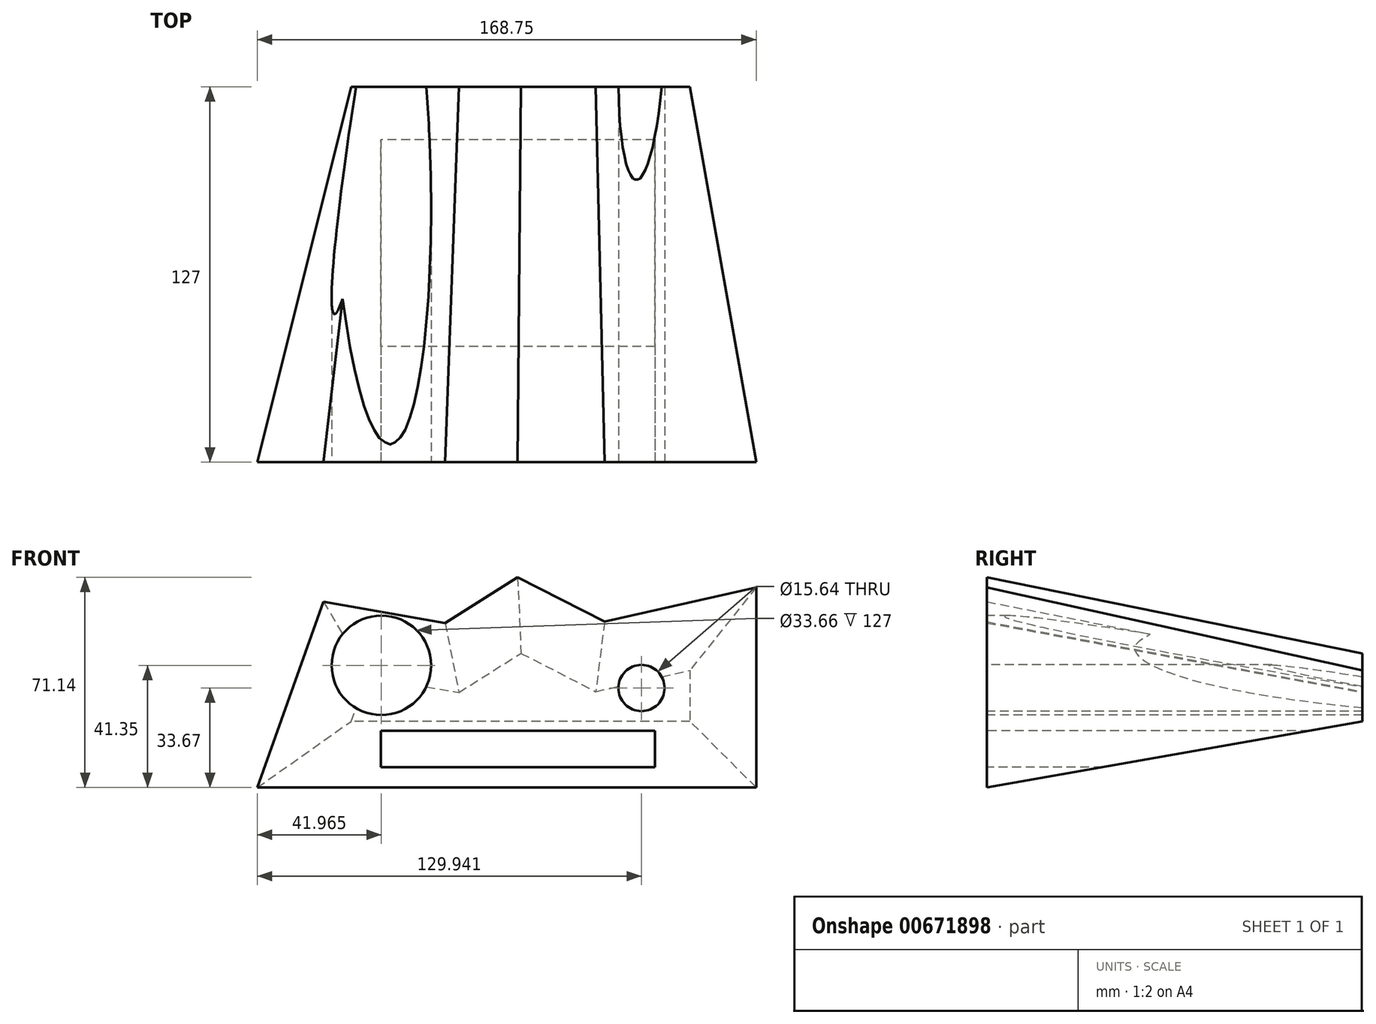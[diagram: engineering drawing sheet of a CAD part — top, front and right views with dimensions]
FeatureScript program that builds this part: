
annotation { "Feature Type Name" : "Feature", "Feature Type Description" : "" }
export const myFeature = defineFeature(function(context is Context, id is Id, definition is map)
    precondition{}
    {
        {
            var Q0;
            Q0=qCreatedBy(makeId("Front.planeOp"),FACE);
            var sketch = newSketch(context, id + "F0", { "sketchPlane" : qUnion([Q0])});
            skLineSegment(sketch, "E0", {"start": v(-47.37, 15.19) * mm, "end": v(-16.4, 9.78) * mm});
            skLineSegment(sketch, "E1", {"start": v(-16.4, 9.78) * mm, "end": v(4.66, 23.01) * mm});
            skLineSegment(sketch, "E2", {"start": v(4.66, 23.01) * mm, "end": v(29.93, 10.08) * mm});
            skLineSegment(sketch, "E3", {"start": v(29.93, 10.08) * mm, "end": v(61.81, 17.3) * mm});
            skLineSegment(sketch, "E4", {"start": v(61.81, 17.3) * mm, "end": v(61.81, 0) * mm});
            skLineSegment(sketch, "E5", {"start": v(61.81, 0) * mm, "end": v(-52.79, 0) * mm});
            skLineSegment(sketch, "E6", {"start": v(-52.79, 0) * mm, "end": v(-47.37, 15.19) * mm});
            skSolve(sketch);
        }
        {
            var Q0;
            Q0=makeQuery(id+"F0.imprint","IMPRINT",FACE,{"disambiguationData":[TD([[makeQuery(id+"F0.imprint","IMPRINT",EDGE,{"derivedFrom":sQuery(id+"F0.wireOp",EDGE,"E0")}),-1.0]])]});
            extrude(context, id + "F1", {"entities" : qUnion([Q0]), "depth" : 127 * mm, "offsetDistance" : 25.4 * mm, "hasDraft" : true, "draftAngle" : 10 * degree});
        }
        {
            var Q0;
            Q0=makeQuery(id+"F1.opExtrude","CAP_FACE",FACE,{"disambiguationData":[OSD([sQuery(id+"F0.wireOp",EDGE,"E0"),sQuery(id+"F0.wireOp",EDGE,"E1"),sQuery(id+"F0.wireOp",EDGE,"E2"),sQuery(id+"F0.wireOp",EDGE,"E3"),sQuery(id+"F0.wireOp",EDGE,"E4"),sQuery(id+"F0.wireOp",EDGE,"E5"),sQuery(id+"F0.wireOp",EDGE,"E6")])],"isStart":false});
            var sketch = newSketch(context, id + "F2", { "sketchPlane" : qUnion([Q0])});
            skCircle(sketch, "E7", {"center": v(45.4, 11.28) * mm, "radius": 7.82 * mm});
            skSolve(sketch);
        }
        {
            var Q0;
            Q0=makeQuery(id+"F2.imprint","IMPRINT",FACE,{"disambiguationData":[TD([[makeQuery(id+"F2.imprint","IMPRINT",EDGE,{"derivedFrom":sQuery(id+"F2.wireOp",EDGE,"E7")}),1.0]])]});
            extrude(context, id + "F3", {"entities" : qUnion([Q0]), "operationType" : NewBodyOperationType.REMOVE, "endBound" : BoundingType.THROUGH_ALL, "oppositeDirection" : true, "depth" : 25.4 * mm, "offsetDistance" : 25.4 * mm});
        }
        {
            var Q0;
            Q0=makeQuery(id+"F1.opExtrude","CAP_FACE",FACE,{"disambiguationData":[OSD([sQuery(id+"F0.wireOp",EDGE,"E0"),sQuery(id+"F0.wireOp",EDGE,"E1"),sQuery(id+"F0.wireOp",EDGE,"E2"),sQuery(id+"F0.wireOp",EDGE,"E3"),sQuery(id+"F0.wireOp",EDGE,"E4"),sQuery(id+"F0.wireOp",EDGE,"E5"),sQuery(id+"F0.wireOp",EDGE,"E6")])],"isStart":false});
            var sketch = newSketch(context, id + "F4", { "sketchPlane" : qUnion([Q0])});
            skCircle(sketch, "E8", {"center": v(-42.57, 18.96) * mm, "radius": 16.83 * mm});
            skSolve(sketch);
        }
        {
            var Q0;
            Q0=makeQuery(id+"F4.imprint","IMPRINT",FACE,{"disambiguationData":[TD([[makeQuery(id+"F4.imprint","IMPRINT",EDGE,{"derivedFrom":sQuery(id+"F4.wireOp",EDGE,"E8")}),1.0]])]});
            extrude(context, id + "F5", {"entities" : qUnion([Q0]), "operationType" : NewBodyOperationType.REMOVE, "endBound" : BoundingType.THROUGH_ALL, "oppositeDirection" : true, "depth" : 25.4 * mm, "offsetDistance" : 25.4 * mm});
        }
        {
            var Q0;
            Q0=makeQuery(id+"F1.opExtrude","CAP_FACE",FACE,{"disambiguationData":[OSD([sQuery(id+"F0.wireOp",EDGE,"E0"),sQuery(id+"F0.wireOp",EDGE,"E1"),sQuery(id+"F0.wireOp",EDGE,"E2"),sQuery(id+"F0.wireOp",EDGE,"E3"),sQuery(id+"F0.wireOp",EDGE,"E4"),sQuery(id+"F0.wireOp",EDGE,"E5"),sQuery(id+"F0.wireOp",EDGE,"E6")])],"isStart":false});
            var sketch = newSketch(context, id + "F6", { "sketchPlane" : qUnion([Q0])});
            skLineSegment(sketch, "E9.bottom", {"start": v(-42.73, -3.16) * mm, "end": v(49.91, -3.16) * mm});
            skLineSegment(sketch, "E9.top", {"start": v(-42.73, -15.5) * mm, "end": v(49.91, -15.5) * mm});
            skLineSegment(sketch, "E9.left", {"start": v(-42.73, -3.16) * mm, "end": v(-42.73, -15.5) * mm});
            skLineSegment(sketch, "E9.right", {"start": v(49.91, -3.16) * mm, "end": v(49.91, -15.5) * mm});
            skSolve(sketch);
        }
        {
            var Q0;
            Q0=makeQuery(id+"F6.imprint","IMPRINT",FACE,{"disambiguationData":[TD([[makeQuery(id+"F6.imprint","IMPRINT",EDGE,{"derivedFrom":sQuery(id+"F6.wireOp",EDGE,"E9.bottom")}),-1.0]])]});
            extrude(context, id + "F7", {"entities" : qUnion([Q0]), "operationType" : NewBodyOperationType.REMOVE, "endBound" : BoundingType.THROUGH_ALL, "oppositeDirection" : true, "depth" : 25.4 * mm, "offsetDistance" : 25.4 * mm});
        }
    });
